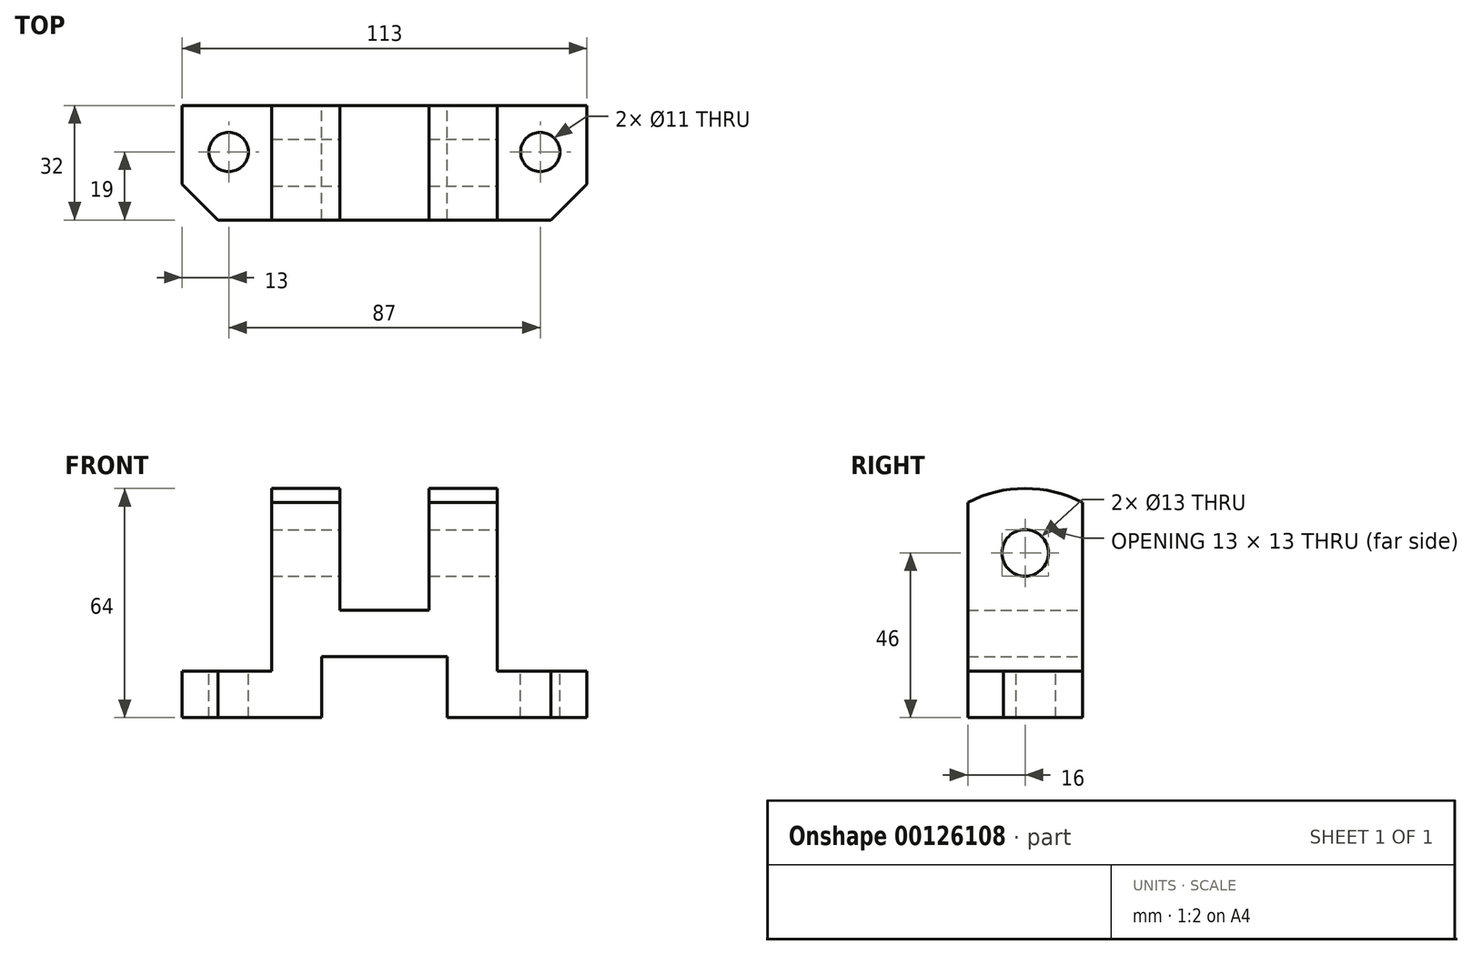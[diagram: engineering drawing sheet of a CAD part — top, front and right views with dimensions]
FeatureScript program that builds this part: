
annotation { "Feature Type Name" : "Feature", "Feature Type Description" : "" }
export const myFeature = defineFeature(function(context is Context, id is Id, definition is map)
    precondition{}
    {
        {
            var Q0;
            Q0=qCreatedBy(makeId("Front.planeOp"),FACE);
            var sketch = newSketch(context, id + "F0", { "sketchPlane" : qUnion([Q0])});
            skLineSegment(sketch, "E0", {"start": v(-56.5, 0) * mm, "end": v(-56.5, 13) * mm});
            skLineSegment(sketch, "E1", {"start": v(-56.5, 13) * mm, "end": v(-31.5, 13) * mm});
            skLineSegment(sketch, "E2", {"start": v(-31.5, 13) * mm, "end": v(-31.5, 64) * mm});
            skLineSegment(sketch, "E3", {"start": v(-31.5, 64) * mm, "end": v(-12.5, 64) * mm});
            skLineSegment(sketch, "E4", {"start": v(-12.5, 64) * mm, "end": v(-12.5, 30) * mm});
            skLineSegment(sketch, "E5", {"start": v(-12.5, 30) * mm, "end": v(12.5, 30) * mm});
            skLineSegment(sketch, "E6", {"start": v(12.5, 30) * mm, "end": v(12.5, 64) * mm});
            skLineSegment(sketch, "E7", {"start": v(12.5, 64) * mm, "end": v(31.5, 64) * mm});
            skLineSegment(sketch, "E8", {"start": v(31.5, 64) * mm, "end": v(31.5, 13) * mm});
            skLineSegment(sketch, "E9", {"start": v(31.5, 13) * mm, "end": v(56.5, 13) * mm});
            skLineSegment(sketch, "E10", {"start": v(56.5, 13) * mm, "end": v(56.5, 0) * mm});
            skLineSegment(sketch, "E11", {"start": v(56.5, 0) * mm, "end": v(-56.5, 0) * mm});
            skLineSegment(sketch, "E12", {"start": v(-17.5, 0) * mm, "end": v(-17.5, 17) * mm});
            skLineSegment(sketch, "E13", {"start": v(-17.5, 17) * mm, "end": v(17.5, 17) * mm});
            skLineSegment(sketch, "E14", {"start": v(17.5, 17) * mm, "end": v(17.5, 0) * mm});
            skSolve(sketch);
        }
        {
            var Q0;
            {var subQ0=sQuery(id+"F0.wireOp",EDGE,"E0");Q0=makeQuery(id+"F0.imprint","IMPRINT",FACE,{"disambiguationData":[TD([[makeQuery(id+"F0.imprint","IMPRINT",EDGE,{"derivedFrom":subQ0}),-1.0]])]});}
            extrude(context, id + "F1", {"entities" : qUnion([Q0]), "depth" : 32 * mm});
        }
        {
            var Q0;
            Q0=makeQuery(id+"F1.opExtrude","SWEPT_FACE",FACE,{"disambiguationData":[OSD([sQuery(id+"F0.wireOp",EDGE,"E9")])]});
            var sketch = newSketch(context, id + "F2", { "sketchPlane" : qUnion([Q0])});
            skLineSegment(sketch, "E15", {"start": v(46.5, -32) * mm, "end": v(56.5, -22) * mm});
            skCircle(sketch, "E16", {"center": v(43.5, -13) * mm, "radius": 5.5 * mm});
            skSolve(sketch);
        }
        {
            var Q0;
            Q0=makeQuery(id+"F1.opExtrude","SWEPT_FACE",FACE,{"disambiguationData":[OSD([sQuery(id+"F0.wireOp",EDGE,"E1")])]});
            var sketch = newSketch(context, id + "F3", { "sketchPlane" : qUnion([Q0])});
            skCircle(sketch, "E17", {"center": v(-43.5, -13) * mm, "radius": 5.5 * mm});
            skLineSegment(sketch, "E18", {"start": v(-56.5, -22) * mm, "end": v(-46.5, -32) * mm});
            skSolve(sketch);
        }
        {
            var Q0;
            Q0=makeQuery(id+"F3.imprint","IMPRINT",FACE,{"disambiguationData":[TD([[makeQuery(id+"F3.imprint","IMPRINT",EDGE,{"derivedFrom":sQuery(id+"F3.wireOp",EDGE,"E17")}),1.0]])]});
            var Q1;
            Q1=makeQuery(id+"F2.imprint","IMPRINT",FACE,{"disambiguationData":[TD([[makeQuery(id+"F2.imprint","IMPRINT",EDGE,{"derivedFrom":sQuery(id+"F2.wireOp",EDGE,"E16")}),1.0]])]});
            var Q2;
            {var subQ0=sQuery(id+"F2.wireOp",EDGE,"E15");Q2=makeQuery(id+"F2.imprint","IMPRINT",FACE,{"disambiguationData":[TD([[makeQuery(id+"F2.imprint","IMPRINT",EDGE,{"derivedFrom":subQ0}),-1.0]])]});}
            var Q3;
            {var subQ0=sQuery(id+"F3.wireOp",EDGE,"E18");Q3=makeQuery(id+"F3.imprint","IMPRINT",FACE,{"disambiguationData":[TD([[makeQuery(id+"F3.imprint","IMPRINT",EDGE,{"derivedFrom":subQ0}),-1.0]])]});}
            extrude(context, id + "F4", {"entities" : qUnion([Q0, Q1, Q2, Q3]), "operationType" : NewBodyOperationType.REMOVE, "endBound" : BoundingType.THROUGH_ALL, "oppositeDirection" : true, "depth" : 25 * mm});
        }
        {
            var Q0;
            Q0=makeQuery(id+"F1.opExtrude","SWEPT_FACE",FACE,{"disambiguationData":[OSD([sQuery(id+"F0.wireOp",EDGE,"E8")])]});
            var sketch = newSketch(context, id + "F5", { "sketchPlane" : qUnion([Q0])});
            skLineSegment(sketch, "E19", {"start": v(-32, 13) * mm, "end": v(-32, 60.13) * mm});
            skLineSegment(sketch, "E20", {"start": v(0, 60.13) * mm, "end": v(0, 13) * mm});
            skArc(sketch, "E21", {"start": v(0, 60.13) * mm, "mid": v(-16, 64) * mm, "end": v(-32, 60.13) * mm});
            skCircle(sketch, "E22", {"center": v(-16, 46) * mm, "radius": 6.5 * mm});
            skLineSegment(sketch, "E23", {"start": v(-16, 13) * mm, "end": v(-16, 64) * mm, "construction": true});
            skSolve(sketch);
        }
        {
            var Q0;
            Q0=makeQuery(id+"F5.imprint","IMPRINT",FACE,{"disambiguationData":[TD([[makeQuery(id+"F5.imprint","IMPRINT",EDGE,{"derivedFrom":sQuery(id+"F5.wireOp",EDGE,"E22")}),1.0]])]});
            var Q1;
            {var subQ0=sQuery(id+"F5.wireOp",EDGE,"E21");var subQ1=sQuery(id+"F0.wireOp",EDGE,"E8");var subQ2=makeQuery(id+"F1.opExtrude","CAP_EDGE",EDGE,{"disambiguationData":[OSD([subQ1])],"isStart":false});var subQ3=makeQuery(id+"F5.imprint","INTERSECT",VERTEX,{"derivedFrom":[subQ2,sQuery(id+"F5.wireOp",EDGE,"E19"),subQ0]});Q1=makeQuery(id+"F5.imprint","IMPRINT",FACE,{"disambiguationData":[TD([[makeQuery(id+"F5.imprint","IMPRINT",EDGE,{"disambiguationData":[TD([[subQ3,1.0]])],"derivedFrom":subQ0}),-1.0]])]});}
            var Q2;
            {var subQ0=sQuery(id+"F5.wireOp",EDGE,"E21");var subQ1=sQuery(id+"F0.wireOp",EDGE,"E8");var subQ2=makeQuery(id+"F1.opExtrude","CAP_EDGE",EDGE,{"disambiguationData":[OSD([subQ1])],"isStart":true});var subQ3=makeQuery(id+"F5.imprint","INTERSECT",VERTEX,{"derivedFrom":[subQ2,sQuery(id+"F5.wireOp",EDGE,"E20"),subQ0]});Q2=makeQuery(id+"F5.imprint","IMPRINT",FACE,{"disambiguationData":[TD([[makeQuery(id+"F5.imprint","IMPRINT",EDGE,{"disambiguationData":[TD([[subQ3,-1.0]])],"derivedFrom":subQ0}),-1.0]])]});}
            extrude(context, id + "F6", {"entities" : qUnion([Q0, Q1, Q2]), "operationType" : NewBodyOperationType.REMOVE, "endBound" : BoundingType.THROUGH_ALL, "oppositeDirection" : true, "depth" : 25 * mm});
        }
    });
